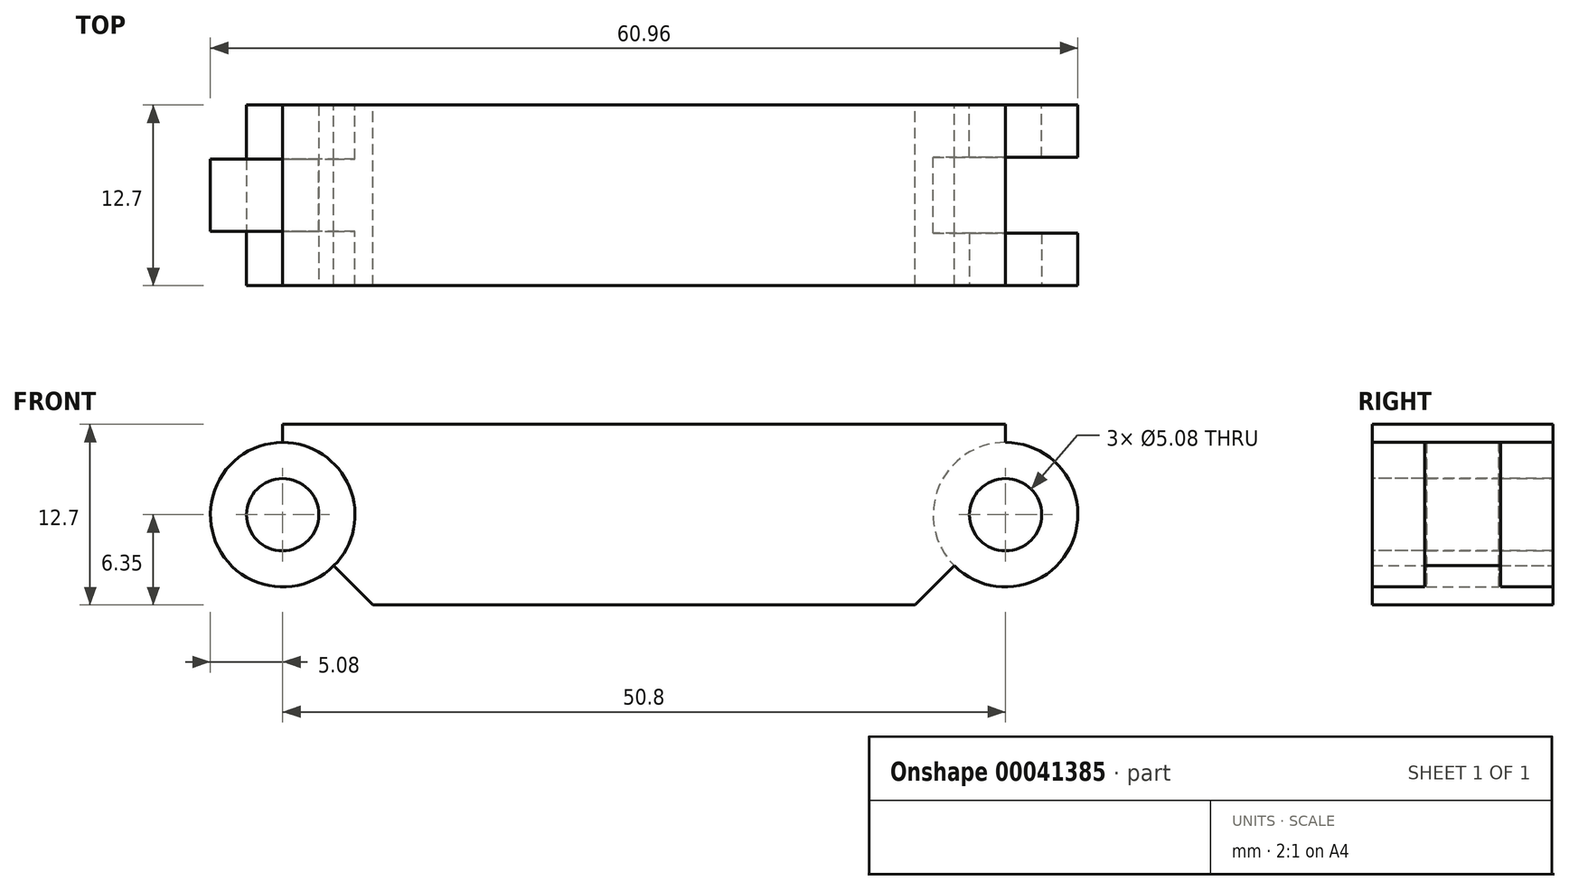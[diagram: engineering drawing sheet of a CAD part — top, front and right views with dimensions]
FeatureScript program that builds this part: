
annotation { "Feature Type Name" : "Feature", "Feature Type Description" : "" }
export const myFeature = defineFeature(function(context is Context, id is Id, definition is map)
    precondition{}
    {
        {
            var Q0;
            Q0=qCreatedBy(makeId("Front.planeOp"),FACE);
            var sketch = newSketch(context, id + "F0", { "sketchPlane" : qUnion([Q0])});
            skLineSegment(sketch, "E0.bottom", {"start": v(0, 12.7) * mm, "end": v(50.8, 12.7) * mm});
            skLineSegment(sketch, "E0.top", {"start": v(0, 0) * mm, "end": v(50.8, 0) * mm});
            skLineSegment(sketch, "E0.left", {"start": v(0, 12.7) * mm, "end": v(0, 0) * mm});
            skLineSegment(sketch, "E0.right", {"start": v(50.8, 12.7) * mm, "end": v(50.8, 0) * mm});
            skCircle(sketch, "E1", {"center": v(0, 6.35) * mm, "radius": 5.08 * mm});
            skCircle(sketch, "E2", {"center": v(0, 6.35) * mm, "radius": 2.54 * mm});
            skLineSegment(sketch, "E3", {"start": v(0, 6.35) * mm, "end": v(6.35, 0) * mm});
            skCircle(sketch, "E4", {"center": v(50.8, 6.35) * mm, "radius": 5.08 * mm});
            skLineSegment(sketch, "E5", {"start": v(50.8, 6.35) * mm, "end": v(44.45, 0) * mm});
            skSolve(sketch);
        }
        {
            var Q0;
            {var subQ12=sQuery(id+"F0.wireOp",EDGE,"E0.bottom");Q0=makeQuery(id+"F0.imprint","IMPRINT",FACE,{"disambiguationData":[TD([[makeQuery(id+"F0.imprint","IMPRINT",EDGE,{"derivedFrom":subQ12}),-1.0]])]});}
            extrude(context, id + "F1", {"entities" : qUnion([Q0]), "endBound" : BoundingType.SYMMETRIC, "depth" : 12.7 * mm});
        }
        {
            var Q0;
            {var subQ1=sQuery(id+"F0.wireOp",EDGE,"E0.left");var subQ4=sQuery(id+"F0.wireOp",EDGE,"E1");var subQ6=makeQuery(id+"F0.imprint","INTERSECT",VERTEX,{"disambiguationData":[OD(0.0)],"derivedFrom":[subQ1,subQ4]});Q0=makeQuery(id+"F0.imprint","IMPRINT",FACE,{"disambiguationData":[TD([[makeQuery(id+"F0.imprint","IMPRINT",EDGE,{"disambiguationData":[TD([[subQ6,-1.0]])],"derivedFrom":subQ1}),-1.0]])]});}
            var Q1;
            {var subQ3=sQuery(id+"F0.wireOp",EDGE,"E0.left");var subQ5=sQuery(id+"F0.wireOp",EDGE,"E1");var subQ7=makeQuery(id+"F0.imprint","INTERSECT",VERTEX,{"disambiguationData":[OD(1.0)],"derivedFrom":[subQ3,subQ5]});Q1=makeQuery(id+"F0.imprint","IMPRINT",FACE,{"disambiguationData":[TD([[makeQuery(id+"F0.imprint","IMPRINT",EDGE,{"disambiguationData":[TD([[subQ7,1.0]])],"derivedFrom":subQ3}),1.0]])]});}
            var Q2;
            {var subQ3=sQuery(id+"F0.wireOp",EDGE,"E0.left");var subQ5=sQuery(id+"F0.wireOp",EDGE,"E1");var subQ7=makeQuery(id+"F0.imprint","INTERSECT",VERTEX,{"disambiguationData":[OD(0.0)],"derivedFrom":[subQ3,subQ5]});Q2=makeQuery(id+"F0.imprint","IMPRINT",FACE,{"disambiguationData":[TD([[makeQuery(id+"F0.imprint","IMPRINT",EDGE,{"disambiguationData":[TD([[subQ7,-1.0]])],"derivedFrom":subQ3}),1.0]])]});}
            extrude(context, id + "F2", {"entities" : qUnion([Q0, Q1, Q2]), "operationType" : NewBodyOperationType.ADD, "endBound" : BoundingType.SYMMETRIC, "depth" : 5.08 * mm});
        }
        {
            var Q0;
            Q0=makeQuery(id+"F1.opExtrude","CAP_FACE",FACE,{"disambiguationData":[OSD([sQuery(id+"F0.wireOp",EDGE,"E0.bottom"),sQuery(id+"F0.wireOp",EDGE,"E0.top"),sQuery(id+"F0.wireOp",EDGE,"E0.left"),sQuery(id+"F0.wireOp",EDGE,"E0.right"),sQuery(id+"F0.wireOp",EDGE,"E1"),sQuery(id+"F0.wireOp",EDGE,"E3"),sQuery(id+"F0.wireOp",EDGE,"E4")])],"isStart":false});
            var sketch = newSketch(context, id + "F3", { "sketchPlane" : qUnion([Q0])});
            skCircle(sketch, "E6", {"center": v(50.8, 6.35) * mm, "radius": 5.08 * mm});
            skCircle(sketch, "E7", {"center": v(50.8, 6.35) * mm, "radius": 2.54 * mm});
            skSolve(sketch);
        }
        {
            var Q0;
            Q0=makeQuery(id+"F3.imprint","IMPRINT",FACE,{"disambiguationData":[TD([[makeQuery(id+"F3.imprint","IMPRINT",EDGE,{"derivedFrom":sQuery(id+"F3.wireOp",EDGE,"E7")}),-1.0]])]});
            extrude(context, id + "F4", {"entities" : qUnion([Q0]), "operationType" : NewBodyOperationType.ADD, "oppositeDirection" : true, "depth" : 3.68 * mm});
        }
        {
            var Q0;
            Q0=makeQuery(id+"F1.opExtrude","CAP_FACE",FACE,{"disambiguationData":[OSD([sQuery(id+"F0.wireOp",EDGE,"E0.bottom"),sQuery(id+"F0.wireOp",EDGE,"E0.top"),sQuery(id+"F0.wireOp",EDGE,"E0.left"),sQuery(id+"F0.wireOp",EDGE,"E0.right"),sQuery(id+"F0.wireOp",EDGE,"E1"),sQuery(id+"F0.wireOp",EDGE,"E3"),sQuery(id+"F0.wireOp",EDGE,"E4")])],"isStart":true});
            var sketch = newSketch(context, id + "F5", { "sketchPlane" : qUnion([Q0])});
            skCircle(sketch, "E8", {"center": v(-50.8, 6.35) * mm, "radius": 5.08 * mm});
            skCircle(sketch, "E9", {"center": v(-50.8, 6.35) * mm, "radius": 2.54 * mm});
            skSolve(sketch);
        }
        {
            var Q0;
            {var subQ0=sQuery(id+"F5.wireOp",EDGE,"E8");Q0=makeQuery(id+"F5.imprint","IMPRINT",FACE,{"disambiguationData":[TD([[makeQuery(id+"F5.imprint","IMPRINT",EDGE,{"disambiguationData":[OD(0.0)],"derivedFrom":subQ0}),1.0]])]});}
            extrude(context, id + "F6", {"entities" : qUnion([Q0]), "operationType" : NewBodyOperationType.ADD, "oppositeDirection" : true, "depth" : 3.68 * mm});
        }
        {
            var Q0;
            Q0=makeQuery(id+"F1.opExtrude","SWEPT_BODY",BODY,{"disambiguationData":[OSD([sQuery(id+"F0.wireOp",EDGE,"E0.bottom"),sQuery(id+"F0.wireOp",EDGE,"E0.top"),sQuery(id+"F0.wireOp",EDGE,"E0.left"),sQuery(id+"F0.wireOp",EDGE,"E0.right"),sQuery(id+"F0.wireOp",EDGE,"E1"),sQuery(id+"F0.wireOp",EDGE,"E3"),sQuery(id+"F0.wireOp",EDGE,"E4"),sQuery(id+"F0.wireOp",EDGE,"E5")])]});
            transform(context, id + "F7", {"entities" : qUnion([Q0]), "transformType" : TransformType.TRANSLATION_3D, "dx" : -50.8 * mm, "dy" : 0 * mm, "dz" : 0 * mm, "makeCopy" : true});
        }
        {
            var Q0;
            Q0=makeQuery(id+"F7.opPattern","COPY",BODY,{"derivedFrom":makeQuery(id+"F1.opExtrude","SWEPT_BODY",BODY,{"disambiguationData":[OSD([sQuery(id+"F0.wireOp",EDGE,"E0.bottom"),sQuery(id+"F0.wireOp",EDGE,"E0.top"),sQuery(id+"F0.wireOp",EDGE,"E0.left"),sQuery(id+"F0.wireOp",EDGE,"E0.right"),sQuery(id+"F0.wireOp",EDGE,"E1"),sQuery(id+"F0.wireOp",EDGE,"E3"),sQuery(id+"F0.wireOp",EDGE,"E4"),sQuery(id+"F0.wireOp",EDGE,"E5")])]}),"instanceName":"1"});
            deleteBodies(context, id + "F8", {"entities" : qUnion([Q0])});
        }
        {
            var Q0;
            Q0=makeQuery(id+"F4.boolean.opBoolean","MERGE",FACE,{"derivedFrom":[makeQuery(id+"F1.opExtrude","CAP_FACE",FACE,{"disambiguationData":[OSD([sQuery(id+"F0.wireOp",EDGE,"E0.bottom"),sQuery(id+"F0.wireOp",EDGE,"E0.top"),sQuery(id+"F0.wireOp",EDGE,"E0.left"),sQuery(id+"F0.wireOp",EDGE,"E0.right"),sQuery(id+"F0.wireOp",EDGE,"E1"),sQuery(id+"F0.wireOp",EDGE,"E3"),sQuery(id+"F0.wireOp",EDGE,"E4"),sQuery(id+"F0.wireOp",EDGE,"E5")])],"isStart":false}),makeQuery(id+"F4.opExtrude","CAP_FACE",FACE,{"disambiguationData":[OSD([sQuery(id+"F3.wireOp",EDGE,"E6"),sQuery(id+"F3.wireOp",EDGE,"E7")])],"isStart":true})]});
            var sketch = newSketch(context, id + "F9", { "sketchPlane" : qUnion([Q0])});
            skCircle(sketch, "E10", {"center": v(0, 6.35) * mm, "radius": 2.54 * mm});
            skSolve(sketch);
        }
        {
            var Q0;
            Q0=makeQuery(id+"F9.imprint","IMPRINT",FACE,{"disambiguationData":[TD([[makeQuery(id+"F9.imprint","IMPRINT",EDGE,{"derivedFrom":sQuery(id+"F9.wireOp",EDGE,"E10")}),1.0]])]});
            extrude(context, id + "F10", {"entities" : qUnion([Q0]), "oppositeDirection" : true, "depth" : 12.7 * mm});
        }
    });
